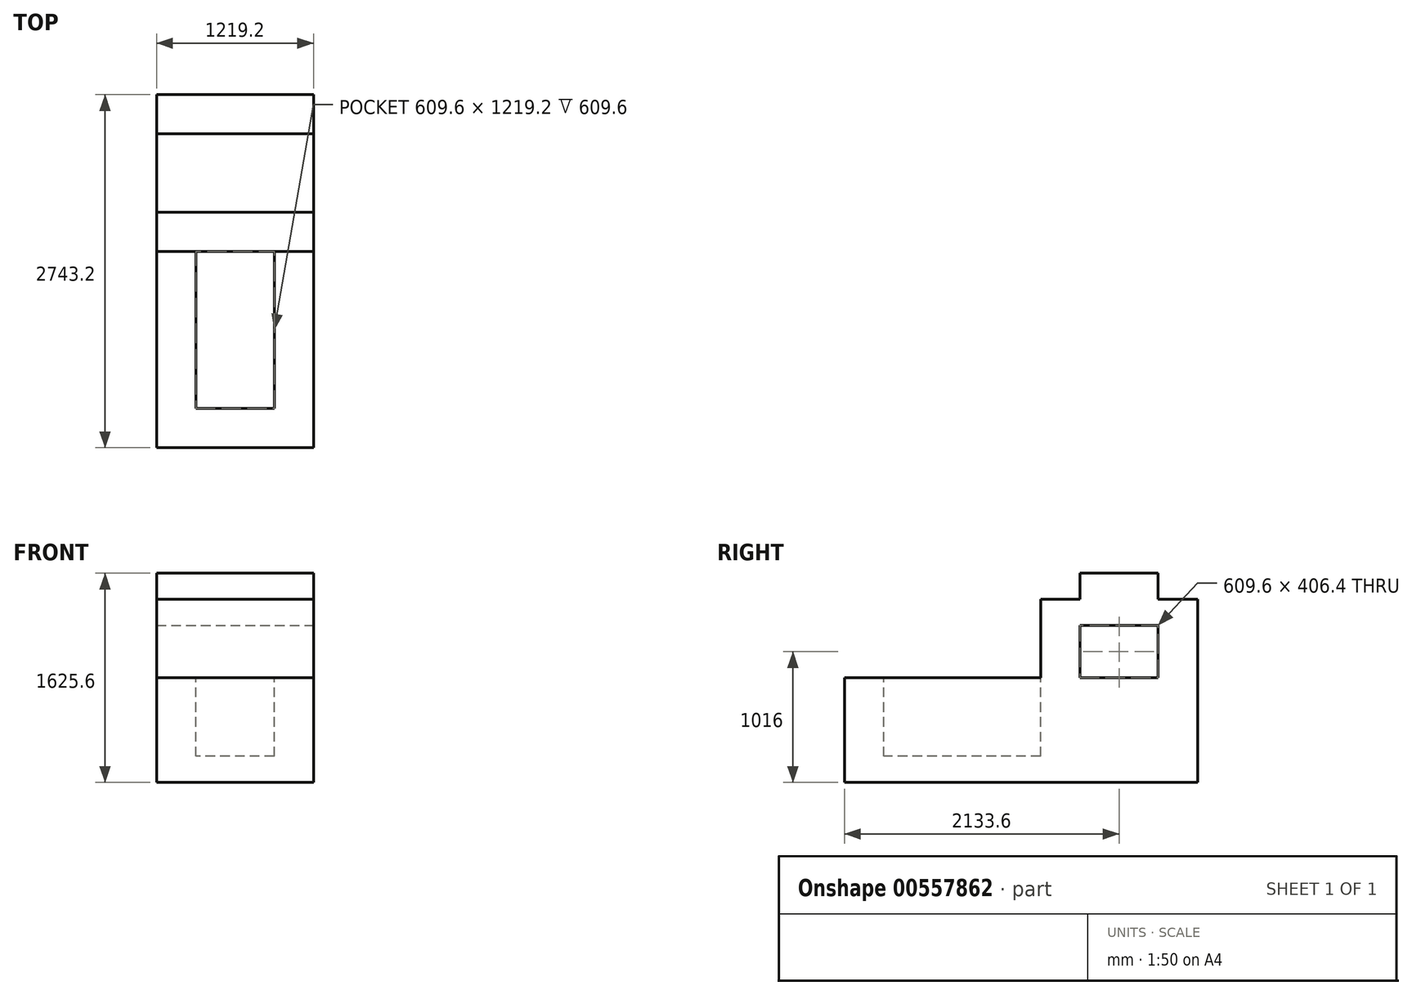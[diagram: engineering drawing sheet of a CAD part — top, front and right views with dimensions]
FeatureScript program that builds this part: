
annotation { "Feature Type Name" : "Feature", "Feature Type Description" : "" }
export const myFeature = defineFeature(function(context is Context, id is Id, definition is map)
    precondition{}
    {
        {
            var Q0;
            Q0=qCreatedBy(makeId("Right.planeOp"),FACE);
            var sketch = newSketch(context, id + "F0", { "sketchPlane" : qUnion([Q0])});
            skLineSegment(sketch, "E0", {"start": v(-58.38, 0) * mm, "end": v(2684.82, 0) * mm});
            skLineSegment(sketch, "E1", {"start": v(2684.82, 0) * mm, "end": v(2684.82, 1422.4) * mm});
            skLineSegment(sketch, "E2", {"start": v(2684.82, 1422.4) * mm, "end": v(2380.02, 1422.4) * mm});
            skLineSegment(sketch, "E3", {"start": v(2380.02, 1422.4) * mm, "end": v(2380.02, 1625.6) * mm});
            skLineSegment(sketch, "E4", {"start": v(2380.02, 1625.6) * mm, "end": v(1770.42, 1625.6) * mm});
            skLineSegment(sketch, "E5", {"start": v(1770.42, 1625.6) * mm, "end": v(1770.42, 1422.4) * mm});
            skLineSegment(sketch, "E6", {"start": v(1770.42, 1422.4) * mm, "end": v(1465.62, 1422.4) * mm});
            skLineSegment(sketch, "E7", {"start": v(1465.62, 1422.4) * mm, "end": v(1465.62, 812.8) * mm});
            skLineSegment(sketch, "E8", {"start": v(1465.62, 812.8) * mm, "end": v(-58.38, 812.8) * mm});
            skLineSegment(sketch, "E9", {"start": v(-58.38, 812.8) * mm, "end": v(-58.38, 0) * mm});
            skSolve(sketch);
        }
        {
            var Q0;
            Q0=makeQuery(id+"F0.imprint","IMPRINT",FACE,{"disambiguationData":[TD([[makeQuery(id+"F0.imprint","IMPRINT",EDGE,{"derivedFrom":sQuery(id+"F0.wireOp",EDGE,"E0")}),1.0]])]});
            extrude(context, id + "F1", {"entities" : qUnion([Q0]), "depth" : 1219.2 * mm, "offsetDistance" : 25.4 * mm});
        }
        {
            var Q0;
            Q0=makeQuery(id+"F1.opExtrude","CAP_FACE",FACE,{"disambiguationData":[OSD([sQuery(id+"F0.wireOp",EDGE,"E0"),sQuery(id+"F0.wireOp",EDGE,"E1"),sQuery(id+"F0.wireOp",EDGE,"E2"),sQuery(id+"F0.wireOp",EDGE,"E3"),sQuery(id+"F0.wireOp",EDGE,"E4"),sQuery(id+"F0.wireOp",EDGE,"E5"),sQuery(id+"F0.wireOp",EDGE,"E6"),sQuery(id+"F0.wireOp",EDGE,"E7"),sQuery(id+"F0.wireOp",EDGE,"E8"),sQuery(id+"F0.wireOp",EDGE,"E9")])],"isStart":false});
            var sketch = newSketch(context, id + "F2", { "sketchPlane" : qUnion([Q0])});
            skLineSegment(sketch, "E10", {"start": v(1770.42, 1219.2) * mm, "end": v(2380.02, 1219.2) * mm});
            skLineSegment(sketch, "E11", {"start": v(2380.02, 1219.2) * mm, "end": v(2380.02, 812.8) * mm});
            skLineSegment(sketch, "E12", {"start": v(2380.02, 812.8) * mm, "end": v(1770.42, 812.8) * mm});
            skLineSegment(sketch, "E13", {"start": v(1770.42, 812.8) * mm, "end": v(1770.42, 1219.2) * mm});
            skSolve(sketch);
        }
        {
            var Q0;
            Q0=makeQuery(id+"F2.imprint","IMPRINT",FACE,{"disambiguationData":[TD([[makeQuery(id+"F2.imprint","IMPRINT",EDGE,{"derivedFrom":sQuery(id+"F2.wireOp",EDGE,"E10")}),-1.0]])]});
            extrude(context, id + "F3", {"entities" : qUnion([Q0]), "operationType" : NewBodyOperationType.REMOVE, "endBound" : BoundingType.THROUGH_ALL, "oppositeDirection" : true, "depth" : 25.4 * mm, "offsetDistance" : 25.4 * mm});
        }
        {
            var Q0;
            Q0=makeQuery(id+"F1.opExtrude","SWEPT_FACE",FACE,{"disambiguationData":[OSD([sQuery(id+"F0.wireOp",EDGE,"E8")])]});
            var sketch = newSketch(context, id + "F4", { "sketchPlane" : qUnion([Q0])});
            skLineSegment(sketch, "E14", {"start": v(304.8, 1465.62) * mm, "end": v(914.4, 1465.62) * mm});
            skLineSegment(sketch, "E15", {"start": v(914.4, 1465.62) * mm, "end": v(914.4, 246.42) * mm});
            skLineSegment(sketch, "E16", {"start": v(914.4, 246.42) * mm, "end": v(304.8, 246.42) * mm});
            skLineSegment(sketch, "E17", {"start": v(304.8, 246.42) * mm, "end": v(304.8, 1465.62) * mm});
            skSolve(sketch);
        }
        {
            var Q0;
            Q0=makeQuery(id+"F4.imprint","IMPRINT",FACE,{"disambiguationData":[TD([[makeQuery(id+"F4.imprint","IMPRINT",EDGE,{"derivedFrom":sQuery(id+"F4.wireOp",EDGE,"E14")}),1.0]])]});
            extrude(context, id + "F5", {"entities" : qUnion([Q0]), "operationType" : NewBodyOperationType.REMOVE, "oppositeDirection" : true, "depth" : 609.6 * mm, "offsetDistance" : 25.4 * mm});
        }
    });
